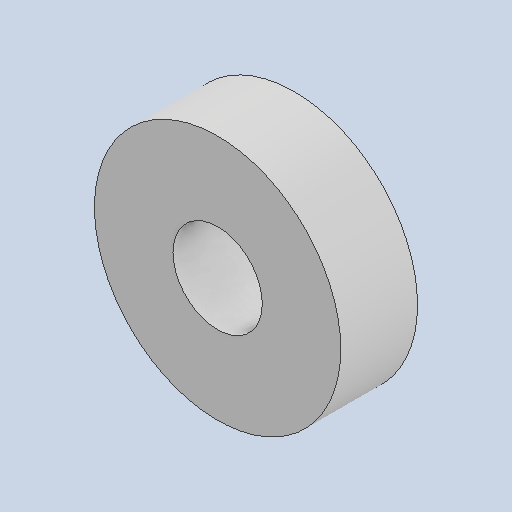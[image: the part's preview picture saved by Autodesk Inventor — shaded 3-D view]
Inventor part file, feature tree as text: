
AUTODESK INVENTOR PART (.ipt)
format: ipt  version: 2023 (Build 270158000, 158)  size: 214,528 bytes
history: native  units: in
note: dims shown in document units (in); Inventor stores cm internally (conversion verified against a paired STEP export)
features: extrude x1, sketch x1
ambient origin geometry x8: Origin, YZ Plane, XZ Plane, XY Plane, X Axis, Y Axis, Z Axis, Center Point
bodies: Solid1 (feature_tree)
feature tree (2):
  extrude  "Extrusion1"  Depth=0.27in
  sketch  "Sketch1"  dims[d0=0.314in d1=0.866in d2=0.27in d3=0.0in]
